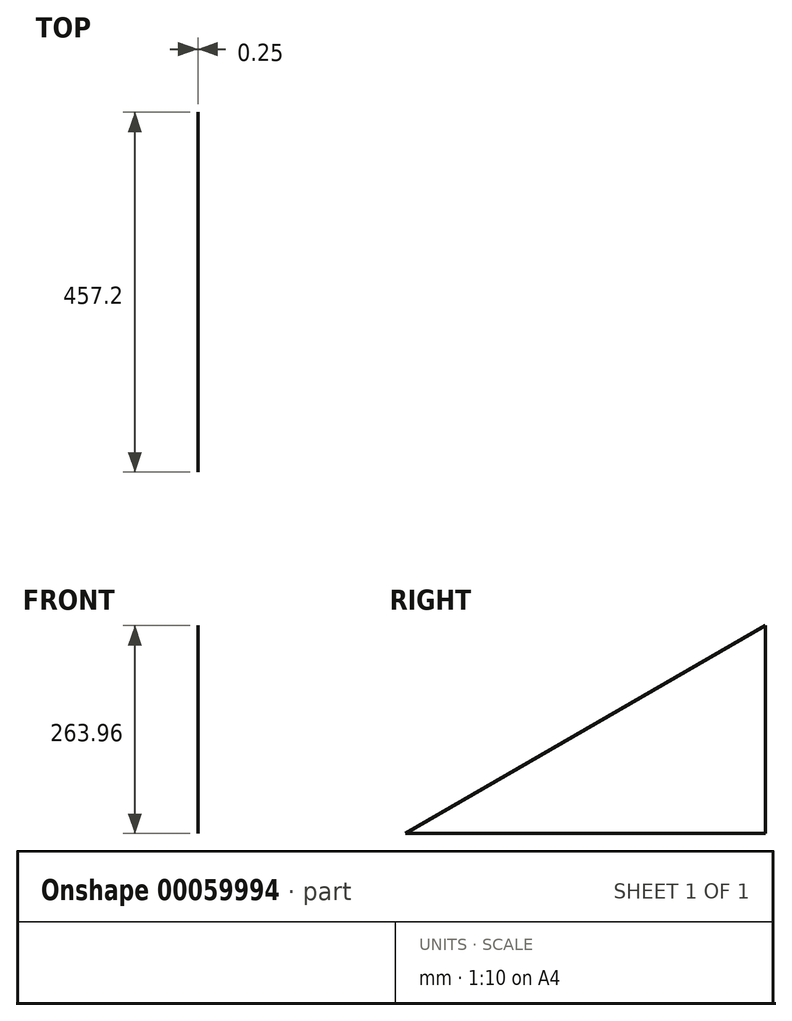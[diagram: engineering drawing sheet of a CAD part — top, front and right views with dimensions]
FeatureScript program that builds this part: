
annotation { "Feature Type Name" : "Feature", "Feature Type Description" : "" }
export const myFeature = defineFeature(function(context is Context, id is Id, definition is map)
    precondition{}
    {
        {
            var Q0;
            Q0=qCreatedBy(makeId("Right.planeOp"),FACE);
            var sketch = newSketch(context, id + "F0", { "sketchPlane" : qUnion([Q0])});
            skLineSegment(sketch, "E0", {"start": v(0, 0) * mm, "end": v(457.2, 263.96) * mm});
            skLineSegment(sketch, "E1", {"start": v(457.2, 263.96) * mm, "end": v(457.2, 0) * mm});
            skLineSegment(sketch, "E2", {"start": v(457.2, 0) * mm, "end": v(0, 0) * mm});
            skSolve(sketch);
        }
        {
            var Q0;
            Q0=makeQuery(id+"F0.imprint","IMPRINT",FACE,{"disambiguationData":[TD([[makeQuery(id+"F0.imprint","IMPRINT",EDGE,{"derivedFrom":sQuery(id+"F0.wireOp",EDGE,"E0")}),-1.0]])]});
            extrude(context, id + "F1", {"entities" : qUnion([Q0]), "depth" : 0.25 * mm});
        }
    });
